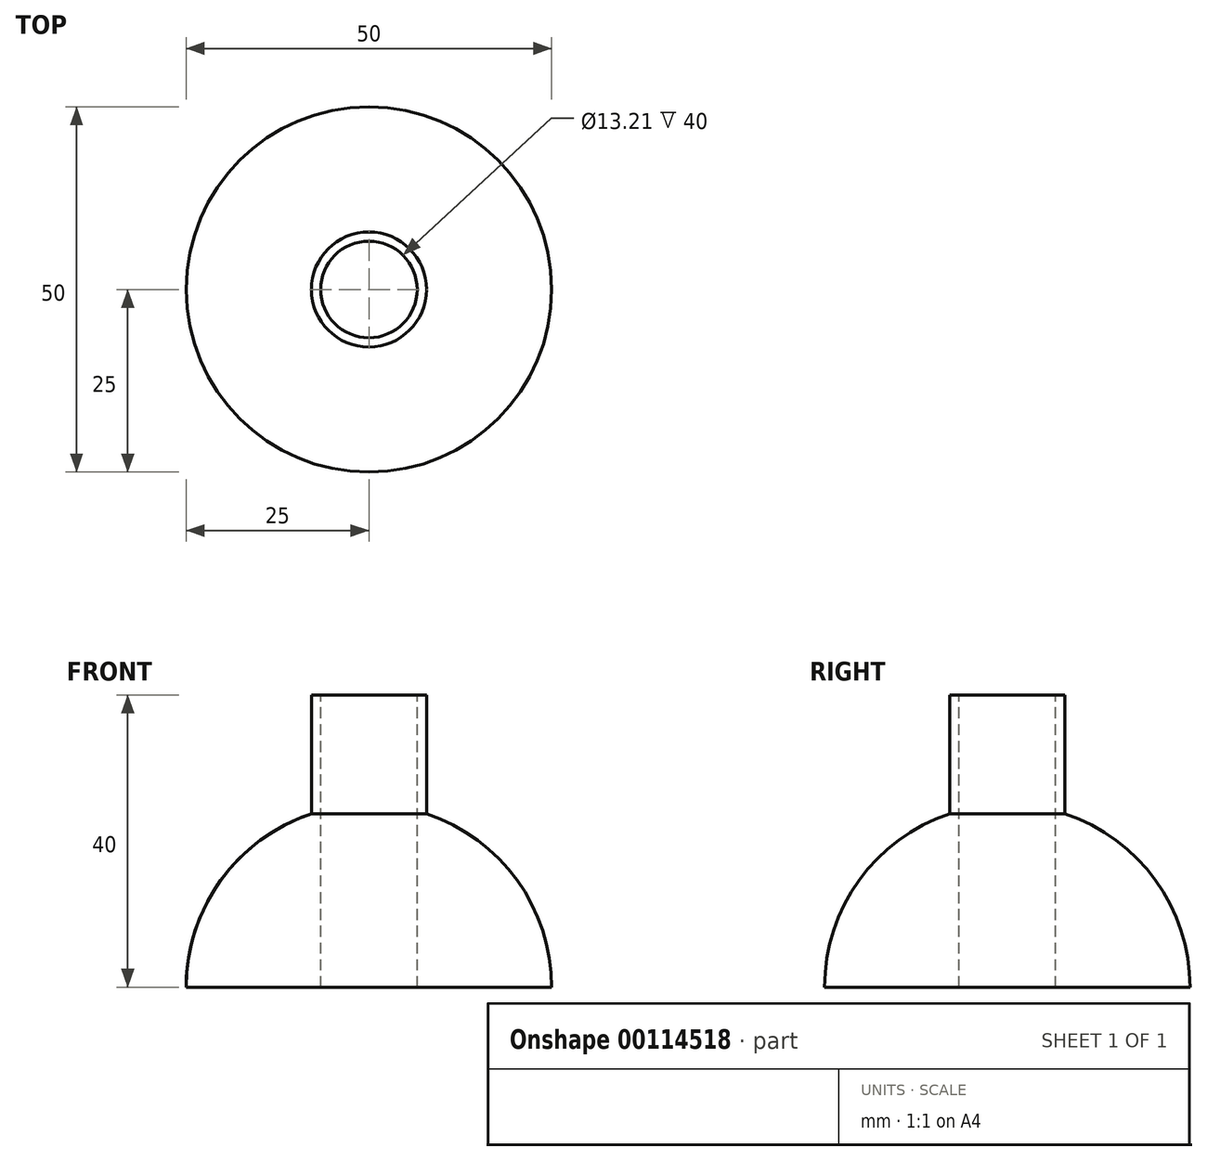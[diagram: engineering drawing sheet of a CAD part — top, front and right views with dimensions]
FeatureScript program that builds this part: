
annotation { "Feature Type Name" : "Feature", "Feature Type Description" : "" }
export const myFeature = defineFeature(function(context is Context, id is Id, definition is map)
    precondition{}
    {
        {
            var Q0;
            Q0=qCreatedBy(makeId("Front.planeOp"),FACE);
            var sketch = newSketch(context, id + "F0", { "sketchPlane" : qUnion([Q0])});
            skArc(sketch, "E0", {"start": v(0, 25) * mm, "mid": v(-17.68, 17.68) * mm, "end": v(-25, 0) * mm});
            skLineSegment(sketch, "E1.bottom", {"start": v(0, 0) * mm, "end": v(-7.87, 0) * mm});
            skLineSegment(sketch, "E1.top", {"start": v(0, 40) * mm, "end": v(-7.87, 40) * mm});
            skLineSegment(sketch, "E1.left", {"start": v(0, 0) * mm, "end": v(0, 40) * mm});
            skLineSegment(sketch, "E1.right", {"start": v(-7.87, 0) * mm, "end": v(-7.87, 40) * mm});
            skLineSegment(sketch, "E2", {"start": v(0, 25) * mm, "end": v(-7.87, 25) * mm});
            skLineSegment(sketch, "E3", {"start": v(-25, 0) * mm, "end": v(0, 0) * mm});
            skSolve(sketch);
        }
        {
            var Q0;
            {var subQ0=sQuery(id+"F0.wireOp",EDGE,"E1.top");Q0=makeQuery(id+"F0.imprint","IMPRINT",FACE,{"disambiguationData":[TD([[makeQuery(id+"F0.imprint","IMPRINT",EDGE,{"derivedFrom":subQ0}),1.0]])]});}
            var Q1;
            {var subQ3=sQuery(id+"F0.wireOp",EDGE,"E1.right");var subQ5=sQuery(id+"F0.wireOp",EDGE,"E3");var subQ7=makeQuery(id+"F0.imprint","INTERSECT",VERTEX,{"derivedFrom":[subQ3,subQ5]});Q1=makeQuery(id+"F0.imprint","IMPRINT",FACE,{"disambiguationData":[TD([[makeQuery(id+"F0.imprint","IMPRINT",EDGE,{"disambiguationData":[TD([[subQ7,-1.0]])],"derivedFrom":subQ3}),-1.0]])]});}
            var Q2;
            {var subQ0=sQuery(id+"F0.wireOp",EDGE,"E3");var subQ1=sQuery(id+"F0.wireOp",EDGE,"E0");var subQ2=makeQuery(id+"F0.imprint","INTERSECT",VERTEX,{"derivedFrom":[subQ1,subQ0]});Q2=makeQuery(id+"F0.imprint","IMPRINT",FACE,{"disambiguationData":[TD([[makeQuery(id+"F0.imprint","IMPRINT",EDGE,{"disambiguationData":[TD([[subQ2,1.0]])],"derivedFrom":subQ1}),1.0]])]});}
            var Q3;
            {var subQ0=sQuery(id+"F0.wireOp",EDGE,"E2");Q3=makeQuery(id+"F0.imprint","IMPRINT",FACE,{"disambiguationData":[TD([[makeQuery(id+"F0.imprint","IMPRINT",EDGE,{"derivedFrom":subQ0}),1.0]])]});}
            var Q4;
            Q4=sQuery(id+"F0.wireOp",EDGE,"E1.left");
            revolve(context, id + "F1", {"entities" : qUnion([Q0, Q1, Q2, Q3]), "axis" : qUnion([Q4]), "revolveType" : RevolveType.FULL});
        }
        {
            var Q0;
            Q0=makeQuery(id+"F1.opRevolve","SWEPT_FACE",FACE,{"disambiguationData":[OSD([sQuery(id+"F0.wireOp",EDGE,"E1.top")])]});
            var sketch = newSketch(context, id + "F2", { "sketchPlane" : qUnion([Q0])});
            skCircle(sketch, "E4", {"center": v(0, 0) * mm, "radius": 6.6 * mm});
            skSolve(sketch);
        }
        {
            var Q0;
            Q0=makeQuery(id+"F2.imprint","IMPRINT",FACE,{"disambiguationData":[TD([[makeQuery(id+"F2.imprint","IMPRINT",EDGE,{"derivedFrom":sQuery(id+"F2.wireOp",EDGE,"E4")}),1.0]])]});
            extrude(context, id + "F3", {"entities" : qUnion([Q0]), "operationType" : NewBodyOperationType.REMOVE, "oppositeDirection" : true, "depth" : 45.8 * mm});
        }
    });
